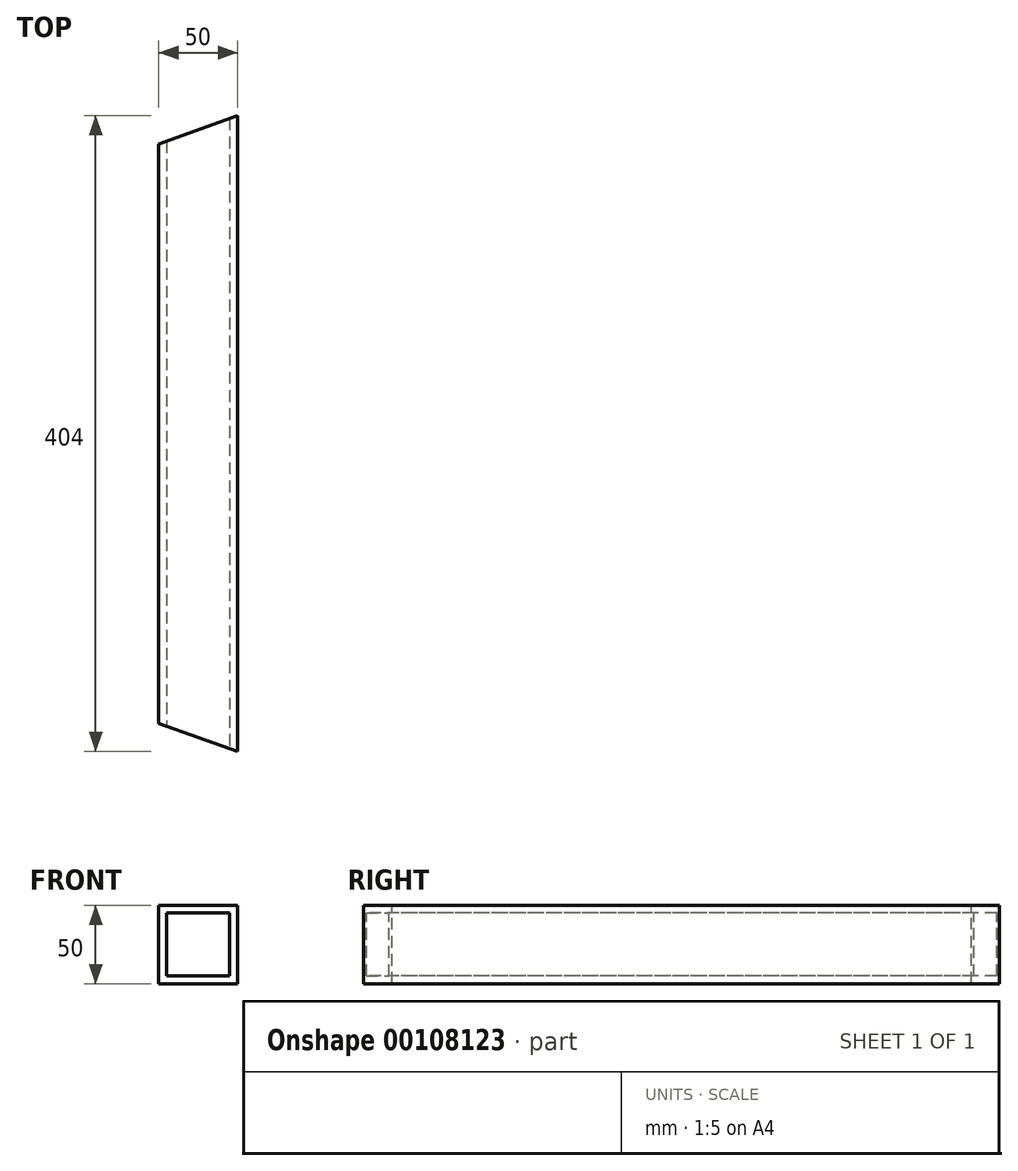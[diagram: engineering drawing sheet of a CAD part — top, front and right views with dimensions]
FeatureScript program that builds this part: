
annotation { "Feature Type Name" : "Feature", "Feature Type Description" : "" }
export const myFeature = defineFeature(function(context is Context, id is Id, definition is map)
    precondition{}
    {
        {
            var Q0;
            Q0=qCreatedBy(makeId("Front.planeOp"),FACE);
            var sketch = newSketch(context, id + "F0", { "sketchPlane" : qUnion([Q0])});
            skLineSegment(sketch, "E0.bottom", {"start": v(25, -25) * mm, "end": v(-25, -25) * mm});
            skLineSegment(sketch, "E0.top", {"start": v(25, 25) * mm, "end": v(-25, 25) * mm});
            skLineSegment(sketch, "E0.left", {"start": v(25, -25) * mm, "end": v(25, 25) * mm});
            skLineSegment(sketch, "E0.right", {"start": v(-25, -25) * mm, "end": v(-25, 25) * mm});
            skPoint(sketch, "E0.middle", {"position": v(0, 0) * mm});
            skLineSegment(sketch, "E1.bottom", {"start": v(20, -20) * mm, "end": v(-20, -20) * mm});
            skLineSegment(sketch, "E1.top", {"start": v(20, 20) * mm, "end": v(-20, 20) * mm});
            skLineSegment(sketch, "E1.left", {"start": v(20, -20) * mm, "end": v(20, 20) * mm});
            skLineSegment(sketch, "E1.right", {"start": v(-20, -20) * mm, "end": v(-20, 20) * mm});
            skSolve(sketch);
        }
        {
            var Q0;
            Q0=makeQuery(id+"F0.imprint","IMPRINT",FACE,{"disambiguationData":[TD([[makeQuery(id+"F0.imprint","IMPRINT",EDGE,{"derivedFrom":sQuery(id+"F0.wireOp",EDGE,"E0.bottom")}),-1.0]])]});
            extrude(context, id + "F1", {"entities" : qUnion([Q0]), "endBound" : BoundingType.SYMMETRIC, "oppositeDirection" : true, "depth" : (202 * 2) * mm});
        }
        {
            var Q0;
            Q0=qCreatedBy(makeId("Top.planeOp"),FACE);
            var sketch = newSketch(context, id + "F2", { "sketchPlane" : qUnion([Q0])});
            skLineSegment(sketch, "E2", {"start": v(25, -202) * mm, "end": v(-25, -184) * mm});
            skLineSegment(sketch, "E3", {"start": v(-25, -184) * mm, "end": v(-25, -202) * mm});
            skLineSegment(sketch, "E4", {"start": v(-25, -202) * mm, "end": v(25, -202) * mm});
            skLineSegment(sketch, "E5", {"start": v(25, 202) * mm, "end": v(-25, 184) * mm});
            skLineSegment(sketch, "E6", {"start": v(-25, 202) * mm, "end": v(25, 202) * mm});
            skLineSegment(sketch, "E7", {"start": v(-25, 202) * mm, "end": v(-25, 184) * mm});
            skLineSegment(sketch, "E8", {"start": v(25, 0) * mm, "end": v(-25, 0) * mm, "construction": true});
            skSolve(sketch);
        }
        {
            var Q0;
            Q0=makeQuery(id+"F2.imprint","IMPRINT",FACE,{"disambiguationData":[TD([[makeQuery(id+"F2.imprint","IMPRINT",EDGE,{"derivedFrom":sQuery(id+"F2.wireOp",EDGE,"E5")}),-1.0]])]});
            var Q1;
            Q1=makeQuery(id+"F2.imprint","IMPRINT",FACE,{"disambiguationData":[TD([[makeQuery(id+"F2.imprint","IMPRINT",EDGE,{"derivedFrom":sQuery(id+"F2.wireOp",EDGE,"E2")}),1.0]])]});
            extrude(context, id + "F3", {"entities" : qUnion([Q0, Q1]), "operationType" : NewBodyOperationType.REMOVE, "endBound" : BoundingType.THROUGH_ALL, "oppositeDirection" : true, "depth" : 25 * mm, "hasSecondDirection" : true, "secondDirectionBound" : SecondDirectionBoundingType.THROUGH_ALL, "secondDirectionOppositeDirection" : false, "secondDirectionDepth" : 25 * mm});
        }
    });
